# Revit family: svetilnik_alfresco_strit-a_dtu-07_os
name_source: partatom
category: Lighting Fixtures
revit_build: Autodesk Revit 2016 (Build: 20150506_1715(x64)
units: mm (PartAtom-declared; Revit-internal decimal feet)

## family parameters
Always vertical = Yes
Cut with Voids When Loaded = No
Light Source = Yes
Part Type = Normal
Room Calculation Point = No
Round Connector Dimension = Use Diameter
Shared = No
Work Plane-Based = No

## types (2) — shared parameters
ADSK_Единица измерения = шт
ADSK_Классификация нагрузок = Освещение
ADSK_Количество фаз = 2
ADSK_Количество фаз числовое = 2
ADSK_Коэффициент мощности = 0.97
ADSK_Масса = 38
ADSK_Модель = Стрит-А(ДТУ-07, ОС)
ADSK_Напряжение = 220 V
ADSK_Размер_Высота = 4150 mm  [stored 13.6155 ft]
ADSK_Размер_Длина = 500 mm  [stored 1.64042 ft]
ADSK_Размер_Ширина = 500 mm  [stored 1.64042 ft]
ADSK_Ток = 0 A
ADSK_Энергоэффективность = 120 lm/W
Color Filter = 16777215
Dimming Lamp Color Temperature Shift = <None>
Dоп = 108 mm
Dсв = 90 mm  [stored 0.295276 ft]
Emit Shape Visible in Rendering = No
Emit from Circle Diameter = 90 mm  [stored 0.295276 ft]
H1 = 3200 mm  [stored 10.4987 ft]
H2 = 900 mm  [stored 2.95276 ft]
IP Class = IP 65
Manufacturer = ALFRESCO
Tilt Angle = 90.00°
URL = http://www.allfresco.ru
Блок аварийного питания = No
Класс Защиты = 1
Класс пожароопасности = F (светильники предназначены для установки непосредственно на поверхность из нормально воспламеняемых матеоиалов)
Климатическая зона = УХЛ1
Материал опоры = Сталь, окрашенная, черная
Область использования = Ландшафт, коттедж.поселки,микрорайоны,АЗС, автостоянки
Сечение по фланцу = 240 mm  [stored 0.787402 ft]
Температура эксплуатации = -35 +40
Тип ИС = LED-светодиоды
Тип КСС = Sym
Тип ПРА = -
Тип продукции = Комплект(Опора освещения+LED светильник)
Цветовая температура = 3000-5500

## per-type parameters (varying)
| type | ADSK_Артикул | ADSK_Наименование | ADSK_Номинальная мощность | ADSK_Полная мощность | Apparent Load | Photometric Web File | Световой поток |
| Стрит А (ДТУ-07, ОС) 35Вт | 1105001650 | Стрит А (ДТУ-07, ОС) 35Вт - св-к СТРИТ-А ДТУ-07-AF (02) на опоре ОС 3,2(d108) ЧМ | 35 W | 36 VA | 36 VA | ДТУ-07-AF Street A 35w.ies | 4200 lm |
| Стрит А (ДТУ-07, ОС) 50Вт | 1105001660 | Стрит А (ДТУ-07, ОС) 50Вт - св-к СТРИТ-А ДТУ-07-AF (02) на опоре ОС 3,2(d108) ЧМ | 50 W | 52 VA | 52 VA | ДТУ-07-AF Street A 50w.ies | 6000 lm |

note: [stored X ft] marks values corroborated as IEEE doubles in the binary element streams (Revit-internal decimal feet)

## geometry (parser evidence)
native form markers: Blend x147
no freeform markers — native parametric forms only
